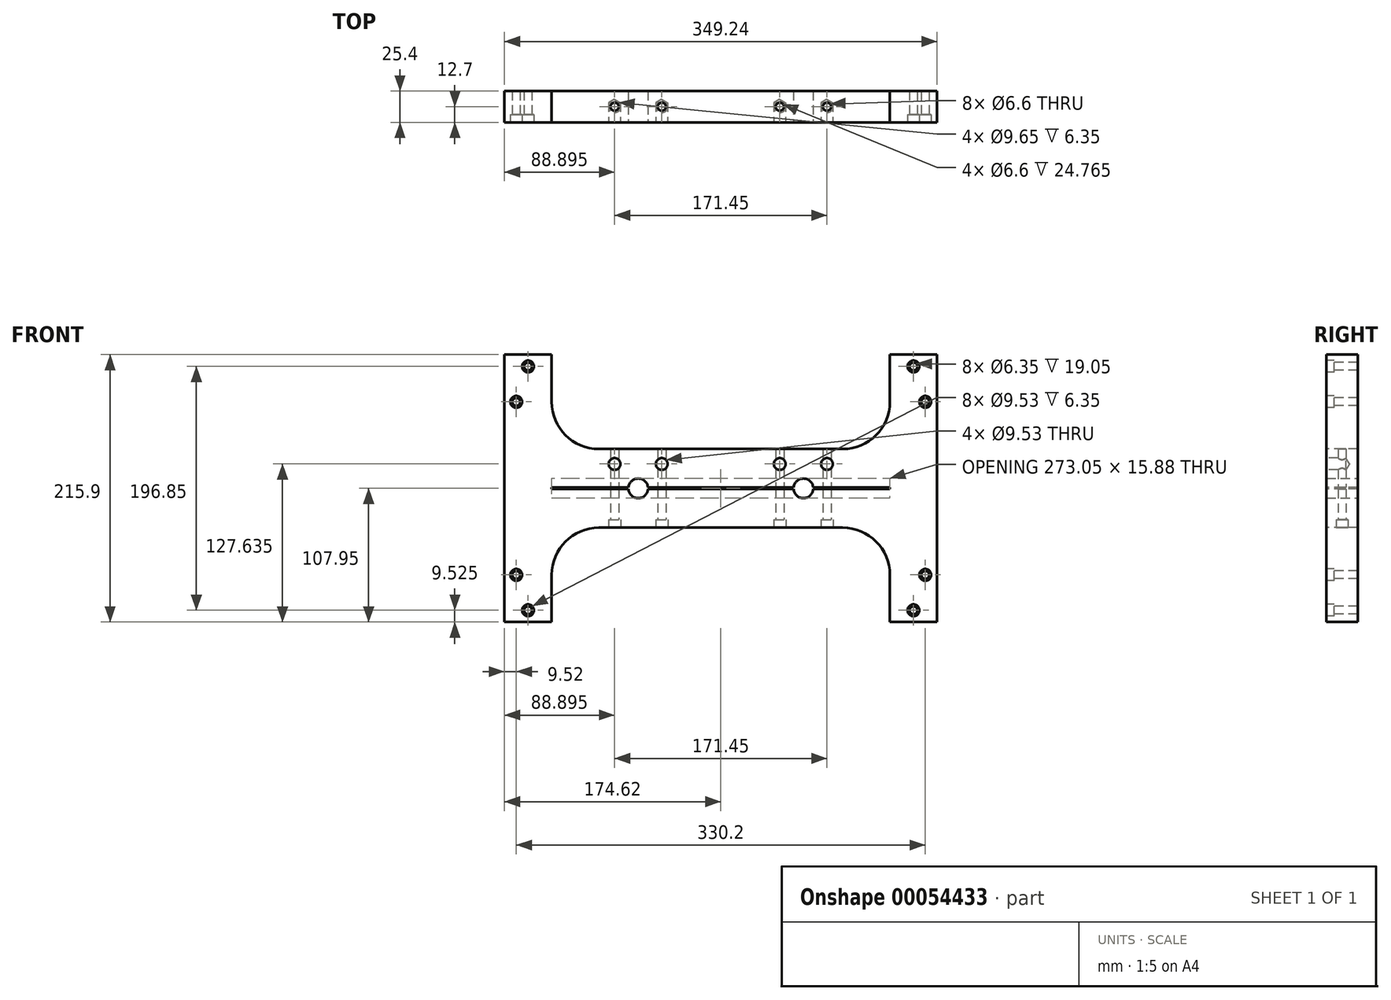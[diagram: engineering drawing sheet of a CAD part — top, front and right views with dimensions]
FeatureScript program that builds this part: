
annotation { "Feature Type Name" : "Feature", "Feature Type Description" : "" }
export const myFeature = defineFeature(function(context is Context, id is Id, definition is map)
    precondition{}
    {
        {
            var Q0;
            Q0=qCreatedBy(makeId("Front.planeOp"),FACE);
            var sketch = newSketch(context, id + "F0", { "sketchPlane" : qUnion([Q0])});
            skLineSegment(sketch, "E0.rect.bottom", {"start": v(-174.63, -107.95) * mm, "end": v(174.63, -107.95) * mm});
            skLineSegment(sketch, "E0.rect.top", {"start": v(-174.63, 107.95) * mm, "end": v(174.63, 107.95) * mm});
            skLineSegment(sketch, "E0.rect.left", {"start": v(-174.63, -107.95) * mm, "end": v(-174.63, 107.95) * mm});
            skLineSegment(sketch, "E0.rect.right", {"start": v(174.63, -107.95) * mm, "end": v(174.63, 107.95) * mm});
            skPoint(sketch, "E0.rect.middle", {"position": v(0, 0) * mm});
            skCircle(sketch, "E1", {"center": v(-66.67, 0) * mm, "radius": 7.94 * mm});
            skLineSegment(sketch, "E2", {"start": v(0, 107.95) * mm, "end": v(0, -107.95) * mm, "construction": true});
            skCircle(sketch, "E3.MirrorC", {"center": v(66.68, 0) * mm, "radius": 7.94 * mm});
            skSolve(sketch);
        }
        {
            var Q0;
            Q0=makeQuery(id+"F0.imprint","IMPRINT",FACE,{"disambiguationData":[TD([[makeQuery(id+"F0.imprint","IMPRINT",EDGE,{"derivedFrom":sQuery(id+"F0.wireOp",EDGE,"E0.rect.bottom")}),1.0]])]});
            extrude(context, id + "F1", {"entities" : qUnion([Q0]), "depth" : 25.4 * mm});
        }
        {
            var Q0;
            Q0=makeQuery(id+"F1.opExtrude","CAP_FACE",FACE,{"disambiguationData":[OSD([sQuery(id+"F0.wireOp",EDGE,"E0.rect.bottom"),sQuery(id+"F0.wireOp",EDGE,"E0.rect.top"),sQuery(id+"F0.wireOp",EDGE,"E0.rect.left"),sQuery(id+"F0.wireOp",EDGE,"E0.rect.right"),sQuery(id+"F0.wireOp",EDGE,"E1"),sQuery(id+"F0.wireOp",EDGE,"E3.MirrorC")])],"isStart":false});
            var sketch = newSketch(context, id + "F2", { "sketchPlane" : qUnion([Q0])});
            skLineSegment(sketch, "E4.bottom", {"start": v(-174.63, 107.95) * mm, "end": v(-136.53, 107.95) * mm});
            skLineSegment(sketch, "E4.top", {"start": v(-174.63, -107.95) * mm, "end": v(-136.52, -107.95) * mm});
            skLineSegment(sketch, "E4.left", {"start": v(-174.63, 107.95) * mm, "end": v(-174.63, -107.95) * mm});
            skLineSegment(sketch, "E4.right", {"start": v(-136.53, 107.95) * mm, "end": v(-136.53, -107.95) * mm});
            skLineSegment(sketch, "E5", {"start": v(0, 107.95) * mm, "end": v(0, -107.95) * mm, "construction": true});
            skLineSegment(sketch, "E6.MirrorCS", {"start": v(136.53, 107.95) * mm, "end": v(136.53, -107.95) * mm});
            skLineSegment(sketch, "E7.MirrorCS", {"start": v(174.63, -107.95) * mm, "end": v(136.53, -107.95) * mm});
            skLineSegment(sketch, "E8.MirrorCS", {"start": v(174.63, 107.95) * mm, "end": v(174.63, -107.95) * mm});
            skLineSegment(sketch, "E9.MirrorCS", {"start": v(174.63, 107.95) * mm, "end": v(136.53, 107.95) * mm});
            skLineSegment(sketch, "E10.rect.bottom", {"start": v(-174.63, -31.75) * mm, "end": v(174.63, -31.75) * mm});
            skLineSegment(sketch, "E10.rect.top", {"start": v(-174.63, 31.75) * mm, "end": v(174.63, 31.75) * mm});
            skLineSegment(sketch, "E10.rect.left", {"start": v(-174.63, -31.75) * mm, "end": v(-174.63, 31.75) * mm});
            skLineSegment(sketch, "E10.rect.right", {"start": v(174.63, -31.75) * mm, "end": v(174.63, 31.75) * mm});
            skPoint(sketch, "E10.rect.middle", {"position": v(0, 0) * mm});
            skLineSegment(sketch, "E11.rect.bottom", {"start": v(-174.63, -0.64) * mm, "end": v(174.63, -0.64) * mm});
            skLineSegment(sketch, "E11.rect.top", {"start": v(-174.63, 0.63) * mm, "end": v(174.63, 0.63) * mm});
            skLineSegment(sketch, "E11.rect.left", {"start": v(-174.63, -0.64) * mm, "end": v(-174.63, 0.63) * mm});
            skLineSegment(sketch, "E11.rect.right", {"start": v(174.63, -0.64) * mm, "end": v(174.63, 0.63) * mm});
            skSolve(sketch);
        }
        {
            var Q0;
            {var subQ0=sQuery(id+"F2.wireOp",EDGE,"E4.right");var subQ3=sQuery(id+"F2.wireOp",EDGE,"E10.rect.bottom");var subQ4=makeQuery(id+"F2.imprint","INTERSECT",VERTEX,{"derivedFrom":[subQ0,subQ3]});Q0=makeQuery(id+"F2.imprint","IMPRINT",FACE,{"disambiguationData":[TD([[makeQuery(id+"F2.imprint","IMPRINT",EDGE,{"disambiguationData":[TD([[subQ4,-1.0]])],"derivedFrom":subQ3}),-1.0]])]});}
            var Q1;
            {var subQ0=sQuery(id+"F2.wireOp",EDGE,"E4.right");var subQ3=sQuery(id+"F2.wireOp",EDGE,"E10.rect.top");var subQ4=makeQuery(id+"F2.imprint","INTERSECT",VERTEX,{"derivedFrom":[subQ0,subQ3]});Q1=makeQuery(id+"F2.imprint","IMPRINT",FACE,{"disambiguationData":[TD([[makeQuery(id+"F2.imprint","IMPRINT",EDGE,{"disambiguationData":[TD([[subQ4,-1.0]])],"derivedFrom":subQ3}),1.0]])]});}
            var Q2;
            {var subQ0=sQuery(id+"F2.wireOp",EDGE,"E11.rect.bottom");var subQ1=makeQuery(id+"F1.opExtrude","CAP_EDGE",EDGE,{"disambiguationData":[OSD([sQuery(id+"F0.wireOp",EDGE,"E1")])],"isStart":false});var subQ2=makeQuery(id+"F2.imprint","INTERSECT",VERTEX,{"disambiguationData":[OD(1.0)],"derivedFrom":[subQ1,subQ0]});Q2=makeQuery(id+"F2.imprint","IMPRINT",FACE,{"disambiguationData":[TD([[makeQuery(id+"F2.imprint","IMPRINT",EDGE,{"disambiguationData":[TD([[subQ2,-1.0]])],"derivedFrom":subQ0}),1.0]])]});}
            var Q3;
            {var subQ0=sQuery(id+"F2.wireOp",EDGE,"E11.rect.top");var subQ1=sQuery(id+"F2.wireOp",EDGE,"E4.right");var subQ2=makeQuery(id+"F2.imprint","INTERSECT",VERTEX,{"derivedFrom":[subQ1,subQ0]});Q3=makeQuery(id+"F2.imprint","IMPRINT",FACE,{"disambiguationData":[TD([[makeQuery(id+"F2.imprint","IMPRINT",EDGE,{"disambiguationData":[TD([[subQ2,-1.0]])],"derivedFrom":subQ1}),1.0]])]});}
            var Q4;
            {var subQ0=sQuery(id+"F2.wireOp",EDGE,"E11.rect.top");var subQ1=sQuery(id+"F2.wireOp",EDGE,"E6.MirrorCS");var subQ2=makeQuery(id+"F2.imprint","INTERSECT",VERTEX,{"derivedFrom":[subQ1,subQ0]});Q4=makeQuery(id+"F2.imprint","IMPRINT",FACE,{"disambiguationData":[TD([[makeQuery(id+"F2.imprint","IMPRINT",EDGE,{"disambiguationData":[TD([[subQ2,-1.0]])],"derivedFrom":subQ1}),-1.0]])]});}
            var Q5;
            {var subQ5=sQuery(id+"F2.wireOp",EDGE,"E11.rect.right");Q5=makeQuery(id+"F2.imprint","IMPRINT",FACE,{"disambiguationData":[TD([[makeQuery(id+"F2.imprint","IMPRINT",EDGE,{"derivedFrom":subQ5}),1.0]])]});}
            var Q6;
            {var subQ5=sQuery(id+"F2.wireOp",EDGE,"E11.rect.left");Q6=makeQuery(id+"F2.imprint","IMPRINT",FACE,{"disambiguationData":[TD([[makeQuery(id+"F2.imprint","IMPRINT",EDGE,{"derivedFrom":subQ5}),-1.0]])]});}
            extrude(context, id + "F3", {"entities" : qUnion([Q0, Q1, Q2, Q3, Q4, Q5, Q6]), "operationType" : NewBodyOperationType.REMOVE, "endBound" : BoundingType.UP_TO_NEXT, "oppositeDirection" : true, "depth" : 25.4 * mm});
        }
        {
            var Q0;
            Q0=makeQuery(id+"F3.boolean.opBoolean","COPY",EDGE,{"derivedFrom":makeQuery(id+"F3.opExtrude","SWEPT_EDGE",EDGE,{"disambiguationData":[OSD([sQuery(id+"F2.wireOp",EDGE,"E4.right"),sQuery(id+"F2.wireOp",EDGE,"E10.rect.top")])]})});
            var Q1;
            Q1=makeQuery(id+"F3.boolean.opBoolean","COPY",EDGE,{"derivedFrom":makeQuery(id+"F3.opExtrude","SWEPT_EDGE",EDGE,{"disambiguationData":[OSD([sQuery(id+"F2.wireOp",EDGE,"E6.MirrorCS"),sQuery(id+"F2.wireOp",EDGE,"E10.rect.top")])]})});
            var Q2;
            Q2=makeQuery(id+"F3.boolean.opBoolean","COPY",EDGE,{"derivedFrom":makeQuery(id+"F3.opExtrude","SWEPT_EDGE",EDGE,{"disambiguationData":[OSD([sQuery(id+"F2.wireOp",EDGE,"E4.right"),sQuery(id+"F2.wireOp",EDGE,"E10.rect.bottom")])]})});
            var Q3;
            Q3=makeQuery(id+"F3.boolean.opBoolean","COPY",EDGE,{"derivedFrom":makeQuery(id+"F3.opExtrude","SWEPT_EDGE",EDGE,{"disambiguationData":[OSD([sQuery(id+"F2.wireOp",EDGE,"E6.MirrorCS"),sQuery(id+"F2.wireOp",EDGE,"E10.rect.bottom")])]})});
            fillet(context, id + "F4", {"entities" : qUnion([Q0, Q1, Q2, Q3]), "radius" : 38.1 * mm, "tangentPropagation" : true, "allowEdgeOverflow" : false});
        }
        {
            var Q0;
            Q0=makeQuery(id+"F3.boolean.opBoolean","COPY",FACE,{"derivedFrom":makeQuery(id+"F3.opExtrude","SWEPT_FACE",FACE,{"disambiguationData":[OSD([sQuery(id+"F2.wireOp",EDGE,"E10.rect.bottom")])]})});
            var sketch = newSketch(context, id + "F5", { "sketchPlane" : qUnion([Q0])});
            skPoint(sketch, "E12", {"position": v(-85.73, 12.7) * mm});
            skPoint(sketch, "E12.positionSnap0", {"position": v(-98.43, 12.7) * mm});
            skPoint(sketch, "E13", {"position": v(-47.63, 12.7) * mm});
            skLineSegment(sketch, "E14", {"start": v(0, 25.4) * mm, "end": v(0, 0) * mm, "construction": true});
            skPoint(sketch, "E15.MirrorP", {"position": v(47.63, 12.7) * mm});
            skPoint(sketch, "E16.MirrorP", {"position": v(85.73, 12.7) * mm});
            skSolve(sketch);
        }
        {
            var Q0;
            Q0=sQuery(id+"F5.wireOp",VERTEX,"E12");
            var Q1;
            Q1=sQuery(id+"F5.wireOp",VERTEX,"E13");
            var Q2;
            Q2=sQuery(id+"F5.wireOp",VERTEX,"E15.MirrorP");
            var Q3;
            Q3=sQuery(id+"F5.wireOp",VERTEX,"E16.MirrorP");
            var Q4;
            Q4=makeQuery(id+"F3.boolean.opBoolean","SPLIT",BODY,{"disambiguationData":[OD(1.0)],"derivedFrom":makeQuery(id+"F1.opExtrude","SWEPT_BODY",BODY,{"disambiguationData":[OSD([sQuery(id+"F0.wireOp",EDGE,"E0.rect.bottom"),sQuery(id+"F0.wireOp",EDGE,"E0.rect.top"),sQuery(id+"F0.wireOp",EDGE,"E0.rect.left"),sQuery(id+"F0.wireOp",EDGE,"E0.rect.right"),sQuery(id+"F0.wireOp",EDGE,"E1"),sQuery(id+"F0.wireOp",EDGE,"E3.MirrorC")])]})});
            hole(context, id + "F6", {"style" : HoleStyle.C_BORE, "holeDiameter" : 6.6 * mm, "cBoreDiameter" : 9.65 * mm, "cBoreDepth" : 6.35 * mm, "endStyle" : HoleEndStyle.THROUGH, "locations" : qUnion([Q0, Q1, Q2, Q3]), "scope" : qUnion([Q4])});
        }
        {
            var Q0;
            {var subQ0=sQuery(id+"F2.wireOp",EDGE,"E11.rect.top");Q0=makeQuery(id+"F3.boolean.opBoolean","COPY",FACE,{"derivedFrom":makeQuery(id+"F3.opExtrude","SWEPT_FACE",FACE,{"disambiguationData":[OSD([subQ0]),TDD([makeQuery(id+"F2.imprint","IMPRINT",EDGE,{"disambiguationData":[TD([[makeQuery(id+"F2.imprint","INTERSECT",VERTEX,{"disambiguationData":[OD(1.0)],"derivedFrom":[makeQuery(id+"F1.opExtrude","CAP_EDGE",EDGE,{"disambiguationData":[OSD([sQuery(id+"F0.wireOp",EDGE,"E1")])],"isStart":false}),subQ0]}),-1.0]])],"derivedFrom":subQ0})])]})});}
            var sketch = newSketch(context, id + "F7", { "sketchPlane" : qUnion([Q0])});
            skPoint(sketch, "E17", {"position": v(-85.73, 12.7) * mm});
            skPoint(sketch, "E17.positionSnap0", {"position": v(-58.76, 12.7) * mm});
            skPoint(sketch, "E18", {"position": v(-47.63, 12.7) * mm});
            skLineSegment(sketch, "E19", {"start": v(0, 25.4) * mm, "end": v(0, 0) * mm, "construction": true});
            skPoint(sketch, "E20.MirrorP", {"position": v(47.63, 12.7) * mm});
            skPoint(sketch, "E21.MirrorP", {"position": v(85.73, 12.7) * mm});
            skSolve(sketch);
        }
        {
            var Q0;
            Q0=sQuery(id+"F7.wireOp",VERTEX,"E17");
            var Q1;
            Q1=sQuery(id+"F7.wireOp",VERTEX,"E18");
            var Q2;
            Q2=sQuery(id+"F7.wireOp",VERTEX,"E20.MirrorP");
            var Q3;
            Q3=sQuery(id+"F7.wireOp",VERTEX,"E21.MirrorP");
            var Q4;
            Q4=makeQuery(id+"F3.boolean.opBoolean","SPLIT",BODY,{"disambiguationData":[OD(0.0)],"derivedFrom":makeQuery(id+"F1.opExtrude","SWEPT_BODY",BODY,{"disambiguationData":[OSD([sQuery(id+"F0.wireOp",EDGE,"E0.rect.bottom"),sQuery(id+"F0.wireOp",EDGE,"E0.rect.top"),sQuery(id+"F0.wireOp",EDGE,"E0.rect.left"),sQuery(id+"F0.wireOp",EDGE,"E0.rect.right"),sQuery(id+"F0.wireOp",EDGE,"E1"),sQuery(id+"F0.wireOp",EDGE,"E3.MirrorC")])]})});
            hole(context, id + "F8", {"style" : HoleStyle.SIMPLE, "holeDiameter" : 6.35 * mm, "endStyle" : HoleEndStyle.BLIND, "holeDepth" : 28.57 * mm, "locations" : qUnion([Q0, Q1, Q2, Q3]), "scope" : qUnion([Q4])});
        }
        {
            var Q0;
            {var subQ2=sQuery(id+"F0.wireOp",EDGE,"E0.rect.top");var subQ5=sQuery(id+"F0.wireOp",EDGE,"E1");var subQ7=sQuery(id+"F0.wireOp",EDGE,"E3.MirrorC");var subQ10=sQuery(id+"F0.wireOp",EDGE,"E0.rect.left");var subQ11=sQuery(id+"F0.wireOp",EDGE,"E0.rect.right");Q0=makeQuery(id+"F3.boolean.opBoolean","SPLIT",FACE,{"disambiguationData":[TD([makeQuery(id+"F1.opExtrude","SWEPT_FACE",FACE,{"disambiguationData":[OSD([subQ2])]})])],"derivedFrom":makeQuery(id+"F1.opExtrude","CAP_FACE",FACE,{"disambiguationData":[OSD([sQuery(id+"F0.wireOp",EDGE,"E0.rect.bottom"),subQ2,subQ10,subQ11,subQ5,subQ7])],"isStart":false})});}
            var sketch = newSketch(context, id + "F9", { "sketchPlane" : qUnion([Q0])});
            skPoint(sketch, "E22", {"position": v(-47.62, 19.68) * mm});
            skPoint(sketch, "E23", {"position": v(-85.72, 19.68) * mm});
            skLineSegment(sketch, "E24", {"start": v(0, 31.75) * mm, "end": v(0, 0) * mm, "construction": true});
            skPoint(sketch, "E25.MirrorP", {"position": v(47.63, 19.68) * mm});
            skPoint(sketch, "E26.MirrorP", {"position": v(85.73, 19.68) * mm});
            skSolve(sketch);
        }
        {
            var Q0;
            Q0=sQuery(id+"F9.wireOp",VERTEX,"E23");
            var Q1;
            Q1=sQuery(id+"F9.wireOp",VERTEX,"E22");
            var Q2;
            Q2=sQuery(id+"F9.wireOp",VERTEX,"E25.MirrorP");
            var Q3;
            Q3=sQuery(id+"F9.wireOp",VERTEX,"E26.MirrorP");
            var Q4;
            Q4=makeQuery(id+"F3.boolean.opBoolean","SPLIT",BODY,{"disambiguationData":[OD(0.0)],"derivedFrom":makeQuery(id+"F1.opExtrude","SWEPT_BODY",BODY,{"disambiguationData":[OSD([sQuery(id+"F0.wireOp",EDGE,"E0.rect.bottom"),sQuery(id+"F0.wireOp",EDGE,"E0.rect.top"),sQuery(id+"F0.wireOp",EDGE,"E0.rect.left"),sQuery(id+"F0.wireOp",EDGE,"E0.rect.right"),sQuery(id+"F0.wireOp",EDGE,"E1"),sQuery(id+"F0.wireOp",EDGE,"E3.MirrorC")])]})});
            hole(context, id + "F10", {"style" : HoleStyle.SIMPLE, "holeDiameter" : 9.52 * mm, "endStyle" : HoleEndStyle.BLIND, "holeDepth" : 15.88 * mm, "locations" : qUnion([Q0, Q1, Q2, Q3]), "scope" : qUnion([Q4])});
        }
        {
            var Q0;
            {var subQ1=sQuery(id+"F0.wireOp",EDGE,"E1");var subQ3=sQuery(id+"F0.wireOp",EDGE,"E3.MirrorC");var subQ8=sQuery(id+"F0.wireOp",EDGE,"E0.rect.bottom");var subQ11=sQuery(id+"F0.wireOp",EDGE,"E0.rect.left");var subQ12=sQuery(id+"F0.wireOp",EDGE,"E0.rect.right");Q0=makeQuery(id+"F3.boolean.opBoolean","SPLIT",FACE,{"disambiguationData":[TD([makeQuery(id+"F1.opExtrude","SWEPT_FACE",FACE,{"disambiguationData":[OSD([subQ8])]})])],"derivedFrom":makeQuery(id+"F1.opExtrude","CAP_FACE",FACE,{"disambiguationData":[OSD([subQ8,sQuery(id+"F0.wireOp",EDGE,"E0.rect.top"),subQ11,subQ12,subQ1,subQ3])],"isStart":false})});}
            var sketch = newSketch(context, id + "F11", { "sketchPlane" : qUnion([Q0])});
            skLineSegment(sketch, "E27.bottom", {"start": v(-174.63, -107.95) * mm, "end": v(-136.53, -107.95) * mm});
            skLineSegment(sketch, "E27.top", {"start": v(-174.63, -88.9) * mm, "end": v(-136.53, -88.9) * mm});
            skLineSegment(sketch, "E27.left", {"start": v(-174.63, -107.95) * mm, "end": v(-174.63, -88.9) * mm});
            skLineSegment(sketch, "E27.right", {"start": v(-136.53, -107.95) * mm, "end": v(-136.53, -88.9) * mm});
            skLineSegment(sketch, "E28.bottom", {"start": v(-174.63, -88.9) * mm, "end": v(-155.58, -88.9) * mm});
            skLineSegment(sketch, "E28.top", {"start": v(-174.63, -50.8) * mm, "end": v(-155.58, -50.8) * mm});
            skLineSegment(sketch, "E28.left", {"start": v(-174.63, -88.9) * mm, "end": v(-174.63, -50.8) * mm});
            skLineSegment(sketch, "E28.right", {"start": v(-155.58, -88.9) * mm, "end": v(-155.58, -50.8) * mm});
            skSolve(sketch);
        }
        {
            var Q0;
            Q0=makeQuery(id+"F11.imprint","IMPRINT",FACE,{"disambiguationData":[TD([[makeQuery(id+"F11.imprint","IMPRINT",EDGE,{"derivedFrom":sQuery(id+"F11.wireOp",EDGE,"E27.bottom")}),1.0]])]});
            var sketch = newSketch(context, id + "F12", { "sketchPlane" : qUnion([Q0])});
            skPoint(sketch, "E29", {"position": v(-155.58, -98.42) * mm});
            skPoint(sketch, "E30", {"position": v(-165.1, -69.85) * mm});
            skLineSegment(sketch, "E31", {"start": v(0, 32.38) * mm, "end": v(0, -31.11) * mm, "construction": true});
            skLineSegment(sketch, "E32", {"start": v(-179.49, 0) * mm, "end": v(-118.37, 0) * mm, "construction": true});
            skPoint(sketch, "E33.MirrorP", {"position": v(-165.1, 69.85) * mm});
            skPoint(sketch, "E34.MirrorP", {"position": v(-155.58, 98.42) * mm});
            skPoint(sketch, "E35.MirrorP", {"position": v(155.58, 98.42) * mm});
            skPoint(sketch, "E36.MirrorP", {"position": v(165.1, 69.85) * mm});
            skPoint(sketch, "E37.MirrorP", {"position": v(165.1, -69.85) * mm});
            skPoint(sketch, "E38.MirrorP", {"position": v(155.58, -98.42) * mm});
            skSolve(sketch);
        }
        {
            var Q0;
            Q0=sQuery(id+"F12.wireOp",VERTEX,"E30");
            var Q1;
            Q1=sQuery(id+"F12.wireOp",VERTEX,"E29");
            var Q2;
            Q2=sQuery(id+"F12.wireOp",VERTEX,"E33.MirrorP");
            var Q3;
            Q3=sQuery(id+"F12.wireOp",VERTEX,"E34.MirrorP");
            var Q4;
            Q4=sQuery(id+"F12.wireOp",VERTEX,"E35.MirrorP");
            var Q5;
            Q5=sQuery(id+"F12.wireOp",VERTEX,"E36.MirrorP");
            var Q6;
            Q6=sQuery(id+"F12.wireOp",VERTEX,"E37.MirrorP");
            var Q7;
            Q7=sQuery(id+"F12.wireOp",VERTEX,"E38.MirrorP");
            var Q8;
            Q8=makeQuery(id+"F3.boolean.opBoolean","SPLIT",BODY,{"disambiguationData":[OD(1.0)],"derivedFrom":makeQuery(id+"F1.opExtrude","SWEPT_BODY",BODY,{"disambiguationData":[OSD([sQuery(id+"F0.wireOp",EDGE,"E0.rect.bottom"),sQuery(id+"F0.wireOp",EDGE,"E0.rect.top"),sQuery(id+"F0.wireOp",EDGE,"E0.rect.left"),sQuery(id+"F0.wireOp",EDGE,"E0.rect.right"),sQuery(id+"F0.wireOp",EDGE,"E1"),sQuery(id+"F0.wireOp",EDGE,"E3.MirrorC")])]})});
            var Q9;
            Q9=makeQuery(id+"F3.boolean.opBoolean","SPLIT",BODY,{"disambiguationData":[OD(0.0)],"derivedFrom":makeQuery(id+"F1.opExtrude","SWEPT_BODY",BODY,{"disambiguationData":[OSD([sQuery(id+"F0.wireOp",EDGE,"E0.rect.bottom"),sQuery(id+"F0.wireOp",EDGE,"E0.rect.top"),sQuery(id+"F0.wireOp",EDGE,"E0.rect.left"),sQuery(id+"F0.wireOp",EDGE,"E0.rect.right"),sQuery(id+"F0.wireOp",EDGE,"E1"),sQuery(id+"F0.wireOp",EDGE,"E3.MirrorC")])]})});
            hole(context, id + "F13", {"style" : HoleStyle.C_BORE, "holeDiameter" : 6.35 * mm, "cBoreDiameter" : 9.52 * mm, "cBoreDepth" : 6.35 * mm, "endStyle" : HoleEndStyle.THROUGH, "locations" : qUnion([Q0, Q1, Q2, Q3, Q4, Q5, Q6, Q7]), "scope" : qUnion([Q8, Q9])});
        }
    });
